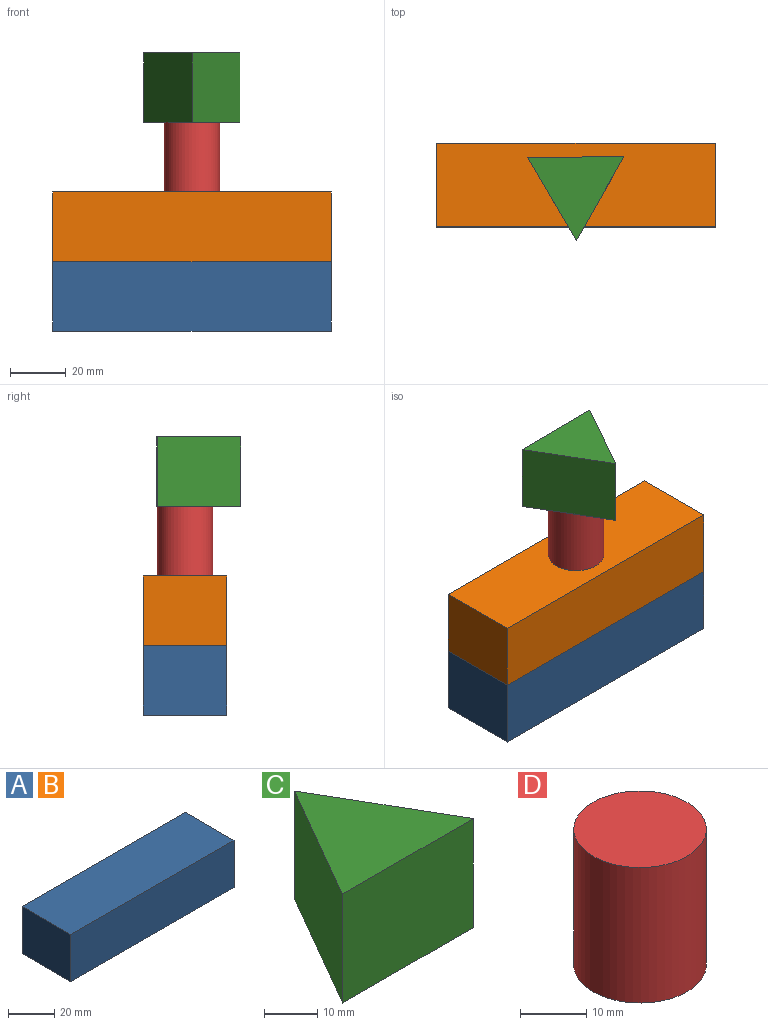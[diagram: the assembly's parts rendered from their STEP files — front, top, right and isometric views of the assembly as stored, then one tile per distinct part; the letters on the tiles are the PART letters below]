
ASSEMBLY  parts=4 mates=3
PART A: 6 faces, bbox 100x30x25 mm
  f0: plane 100x25mm, normal (0,-1,0), area 2500mm2, adj f1,f3,f4,f5
  f1: plane 30x25mm, normal (1,0,0), area 750mm2, adj f0,f2,f4,f5
  f2: plane 100x25mm, normal (0,1,0), area 2500mm2, adj f1,f3,f4,f5
  f3: plane 30x25mm, normal (-1,0,0), area 750mm2, adj f0,f2,f4,f5
  f4: plane 100x30mm, normal (0,0,1), area 3000mm2, adj f0,f1,f2,f3
  f5: plane 100x30mm, normal (0,0,-1), area 3000mm2, adj f0,f1,f2,f3
PART B: same geometry as A
PART C: 5 faces, bbox 34.6x30x25 mm
  f0: plane 34.64x25mm, normal (0,-1,0), area 866mm2, adj f1,f2,f3,f4
  f1: plane 30x25mm, normal (0.87,0.5,0), area 866mm2, adj f0,f2,f3,f4
  f2: plane 30x25mm, normal (-0.87,0.5,0), area 866mm2, adj f0,f1,f3,f4
  f3: plane 34.64x30mm, normal (0,0,1), area 519.6mm2, adj f0,f1,f2
  f4: plane 34.64x30mm, normal (0,0,-1), area 519.6mm2, adj f0,f1,f2
PART D: 3 faces, bbox 20x20x25 mm
  f0: cylinder r=10mm len=25mm, axis (0,0,-1), area 1570.8mm2, adj f1,f2
  f1: plane 20x20mm, normal (0,0,1), area 314.2mm2, adj f0
  f2: plane 20x20mm, normal (0,0,-1), area 314.2mm2, adj f0
PLACE A t=(0,0,-25)mm
PLACE B at identity fixed
PLACE C rot(axis=(0,0,-1),59.6deg) t=(15.2,-25.87,0)mm
PLACE D rot(axis=(-0.96,-0.26,0),180deg) t=(25.87,15.2,75)mm
MATE fastened C.f4 <-> D.f0  axis (0,0,-1) through (0,0,50)mm
MATE revolute B.f4 <-> D.f0  axis (0,0,1) through (0,0,25)mm
MATE slider B.f3 <-> A.f3  axis (-1,0,0) through (-50,0,0)mm
